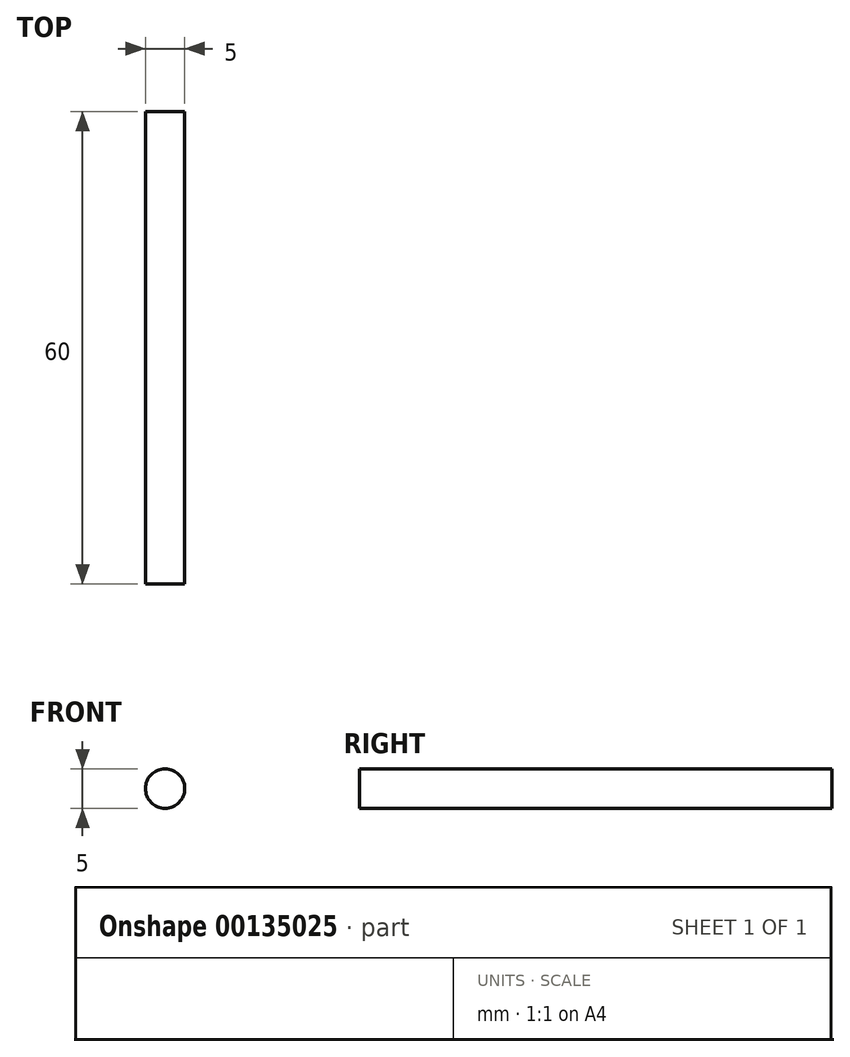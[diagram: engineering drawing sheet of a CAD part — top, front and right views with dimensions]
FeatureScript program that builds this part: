
annotation { "Feature Type Name" : "Feature", "Feature Type Description" : "" }
export const myFeature = defineFeature(function(context is Context, id is Id, definition is map)
    precondition{}
    {
        {
            var Q0;
            Q0=qCreatedBy(makeId("Front.planeOp"),FACE);
            var sketch = newSketch(context, id + "F0", { "sketchPlane" : qUnion([Q0])});
            skCircle(sketch, "E0", {"center": v(0, 0) * mm, "radius": 2.5 * mm});
            skSolve(sketch);
        }
        {
            var Q0;
            Q0 = qSketchRegion(id + "F0", true);
            extrude(context, id + "F1", {"entities" : qUnion([Q0]), "depth" : 60 * mm});
        }
    });
